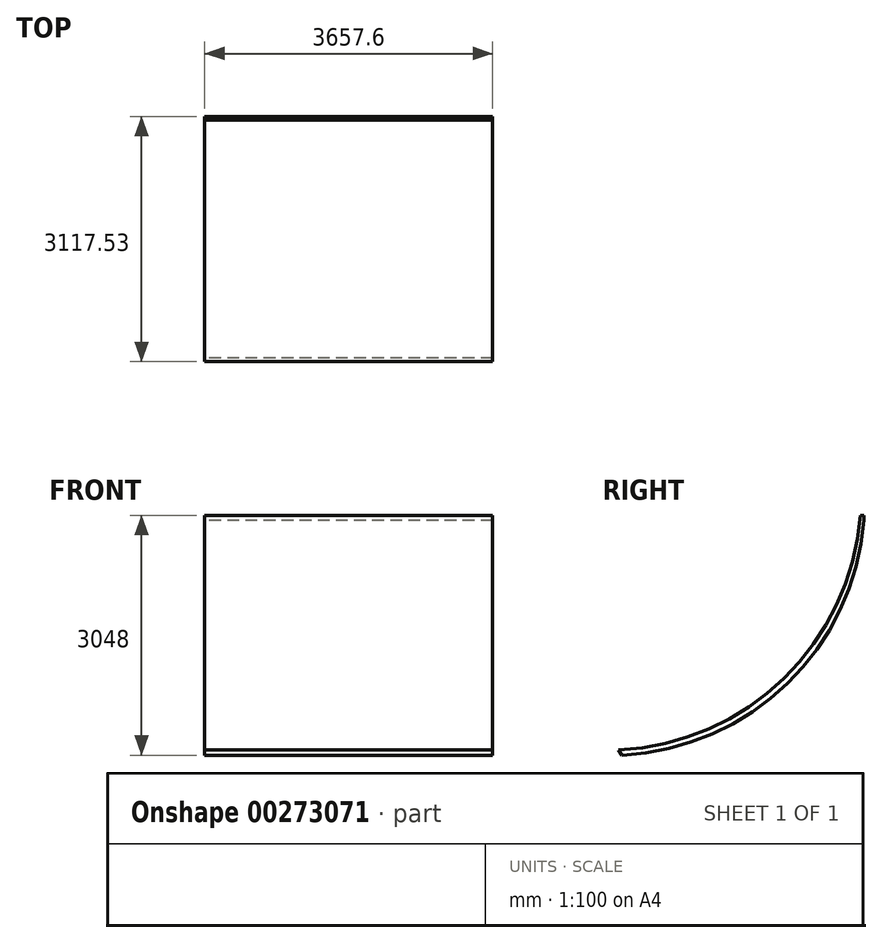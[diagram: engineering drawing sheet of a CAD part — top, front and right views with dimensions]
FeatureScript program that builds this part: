
annotation { "Feature Type Name" : "Feature", "Feature Type Description" : "" }
export const myFeature = defineFeature(function(context is Context, id is Id, definition is map)
    precondition{}
    {
        {
            var Q0;
            Q0=qCreatedBy(makeId("Right.planeOp"),FACE);
            var sketch = newSketch(context, id + "F0", { "sketchPlane" : qUnion([Q0])});
            skArc(sketch, "E0", {"start": v(-3071.21, -2056.45) * mm, "mid": v(-971.84, -1144.9) * mm, "end": v(0, 927.24) * mm});
            skArc(sketch, "E1", {"start": v(-3026.64, -2120.76) * mm, "mid": v(-927.28, -1209.21) * mm, "end": v(44.57, 862.93) * mm});
            skLineSegment(sketch, "E2", {"start": v(-3071.21, -2056.45) * mm, "end": v(-3026.64, -2120.76) * mm});
            skLineSegment(sketch, "E3", {"start": v(0, 927.24) * mm, "end": v(46.32, 927.24) * mm});
            skLineSegment(sketch, "E4", {"start": v(46.32, 927.24) * mm, "end": v(44.57, 862.93) * mm});
            skSolve(sketch);
        }
        {
            var Q0;
            Q0 = qSketchRegion(id + "F0", true);
            extrude(context, id + "F1", {"entities" : qUnion([Q0]), "depth" : 3657.6 * mm});
        }
    });
